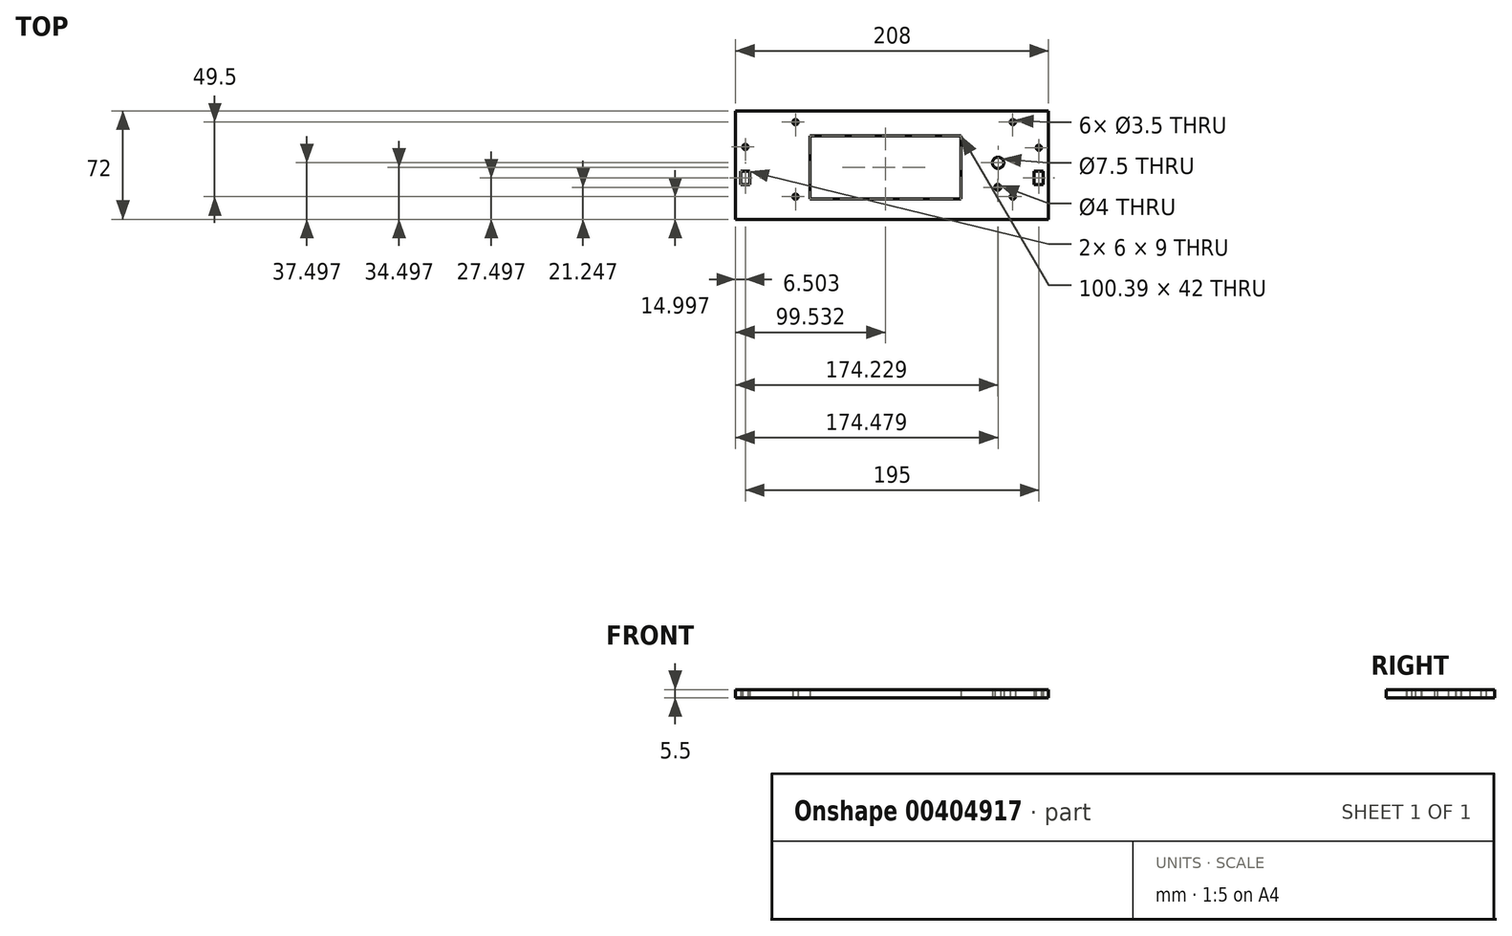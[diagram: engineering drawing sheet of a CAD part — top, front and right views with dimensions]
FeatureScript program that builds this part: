
annotation { "Feature Type Name" : "Feature", "Feature Type Description" : "" }
export const myFeature = defineFeature(function(context is Context, id is Id, definition is map)
    precondition{}
    {
        {
            var Q0;
            Q0=qCreatedBy(makeId("Top.planeOp"),FACE);
            var sketch = newSketch(context, id + "F0", { "sketchPlane" : qUnion([Q0])});
            skLineSegment(sketch, "E0.bottom", {"start": v(-112.4, 29.26) * mm, "end": v(95.6, 29.26) * mm});
            skLineSegment(sketch, "E0.top", {"start": v(-112.4, -42.74) * mm, "end": v(95.6, -42.74) * mm});
            skLineSegment(sketch, "E0.left", {"start": v(-112.4, 29.26) * mm, "end": v(-112.4, -42.74) * mm});
            skLineSegment(sketch, "E0.right", {"start": v(95.6, 29.26) * mm, "end": v(95.6, -42.74) * mm});
            skLineSegment(sketch, "E1.bottom", {"start": v(-63.06, 12.76) * mm, "end": v(37.33, 12.76) * mm});
            skLineSegment(sketch, "E1.top", {"start": v(-63.06, -29.24) * mm, "end": v(37.33, -29.24) * mm});
            skLineSegment(sketch, "E1.left", {"start": v(-63.06, 12.76) * mm, "end": v(-63.06, -29.24) * mm});
            skLineSegment(sketch, "E1.right", {"start": v(37.33, 12.76) * mm, "end": v(37.33, -29.24) * mm});
            skCircle(sketch, "E2", {"center": v(62.08, -5.24) * mm, "radius": 3.75 * mm});
            skCircle(sketch, "E3", {"center": v(61.83, -21.5) * mm, "radius": 2 * mm});
            skCircle(sketch, "E4", {"center": v(-72.56, 21.76) * mm, "radius": 1.75 * mm});
            skCircle(sketch, "E5", {"center": v(-72.56, -27.74) * mm, "radius": 1.75 * mm});
            skCircle(sketch, "E6", {"center": v(71.83, -27.74) * mm, "radius": 1.75 * mm});
            skCircle(sketch, "E7", {"center": v(71.83, 21.76) * mm, "radius": 1.75 * mm});
            skCircle(sketch, "E8", {"center": v(-105.9, 5.26) * mm, "radius": 1.75 * mm});
            skLineSegment(sketch, "E9", {"start": v(-105.9, -10.74) * mm, "end": v(-105.9, 13.54) * mm, "construction": true});
            skLineSegment(sketch, "E10", {"start": v(89.1, -10.74) * mm, "end": v(89.1, 20.26) * mm, "construction": true});
            skCircle(sketch, "E11", {"center": v(89.1, 4.76) * mm, "radius": 1.75 * mm, "construction": true});
            skCircle(sketch, "E12", {"center": v(89.1, 4.76) * mm, "radius": 1.75 * mm});
            skLineSegment(sketch, "E13.bottom", {"start": v(-102.9, -19.74) * mm, "end": v(-108.9, -19.74) * mm});
            skLineSegment(sketch, "E13.top", {"start": v(-102.9, -10.74) * mm, "end": v(-108.9, -10.74) * mm});
            skLineSegment(sketch, "E13.left", {"start": v(-102.9, -19.74) * mm, "end": v(-102.9, -10.74) * mm});
            skLineSegment(sketch, "E13.right", {"start": v(-108.9, -19.74) * mm, "end": v(-108.9, -10.74) * mm});
            skLineSegment(sketch, "E14.bottom", {"start": v(86.1, -10.74) * mm, "end": v(92.1, -10.74) * mm});
            skLineSegment(sketch, "E14.top", {"start": v(86.1, -19.74) * mm, "end": v(92.1, -19.74) * mm});
            skLineSegment(sketch, "E14.left", {"start": v(86.1, -10.74) * mm, "end": v(86.1, -19.74) * mm});
            skLineSegment(sketch, "E14.right", {"start": v(92.1, -10.74) * mm, "end": v(92.1, -19.74) * mm});
            skSolve(sketch);
        }
        {
            var Q0;
            {var subQ7=sQuery(id+"F0.wireOp",EDGE,"E0.bottom");Q0=makeQuery(id+"F0.imprint","IMPRINT",FACE,{"disambiguationData":[TD([[makeQuery(id+"F0.imprint","IMPRINT",EDGE,{"derivedFrom":subQ7}),-1.0]])]});}
            extrude(context, id + "F1", {"entities" : qUnion([Q0]), "depth" : 5.5 * mm});
        }
    });
